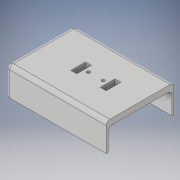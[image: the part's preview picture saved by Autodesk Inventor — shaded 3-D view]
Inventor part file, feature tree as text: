
AUTODESK INVENTOR PART (.ipt)
format: ipt  version: 2019 (Build 230136000, 136)  size: 304,640 bytes
history: native  units: in
note: dims shown in document units (in); Inventor stores cm internally (conversion verified against a paired STEP export)
features: sketch x12, extrude x10, projected_geometry x5, fillet x3, plane x2, emboss x1
ambient origin geometry x8: Origin, YZ Plane, XZ Plane, XY Plane, X Axis, Y Axis, Z Axis, Center Point
bodies: Solid1 (feature_tree)
feature tree (33):
  extrude  "Extrusion1"  Depth=3.4in
  extrude  "Extrusion6"  Depth=0.2in TaperAngle=0.0deg
  plane  "Work Plane1"
  extrude  "Extrusion7"  Depth=3.25in TaperAngle=0.0deg
  extrude  "Extrusion9"  Depth=0.15in TaperAngle=0.0deg
  extrude  "Extrusion12"  Depth=0.2in TaperAngle=0.0deg
  fillet  "Fillet7"  Radius=0.66in
  extrude  "Extrusion13"  Depth=0.2in TaperAngle=0.0deg
  extrude  "Extrusion14"  Depth=0.05in TaperAngle=0.0deg
  emboss  "Emboss2"
  plane  "Work Plane2"
  extrude  "Extrusion15"  Depth=0.125in
  sketch  "Sketch21"  dims[d92=0.7874in d94=1.0in d95=0.3937in d97=1.0in d99=0.05in d100=0.0in]
  extrude  "Extrusion16"  Depth=1.0in
  fillet  "Fillet10"  Radius=0.05in
  extrude  "Extrusion17"  Depth=0.25in
  fillet  "Fillet11"  Radius=0.25in
  sketch  "Sketch1"  dims[d0=2.3in d1=3.4in]
  sketch  "Sketch9"  dims[d2=0.5in d3=0.0in d23=0.2in d24=0.0in]
  projected_geometry  "Projected Loop4"
  sketch  "Sketch10"  dims[d26=0.4in d31=3.25in d32=0.0in]
  sketch  "Sketch12"  dims[d42=0.4in d43=0.0in d57=0.15in d58=0.0in]
  sketch  "Sketch16"  dims[d59=0.125in d60=0.2in d61=0.0in d62=0.66in d63=0.0in]
  sketch  "Sketch17"  dims[d65=0.05in d66=0.0in d74=0.2in d75=0.0in]
  projected_geometry  "Projected Loop7"
  sketch  "Sketch18"  dims[d77=0.3in d79=0.05in d80=0.0in]
  projected_geometry  "Projected Loop8"
  sketch  "Sketch19"  dims[d81=0.125in d89=0.5in]
  sketch  "Sketch20"  dims[d90=0.2in d91=1.0in]
  projected_geometry  "Projected Loop9"
  sketch  "Sketch22"  dims[d101=0.1094in d102=0.25in d103=0.25in]
  projected_geometry  "Projected Loop10"
  sketch  "Sketch23"  dims[d104=0.45in d105=0.07in d106=0.07in d107=0.15in d108=0.125in]
